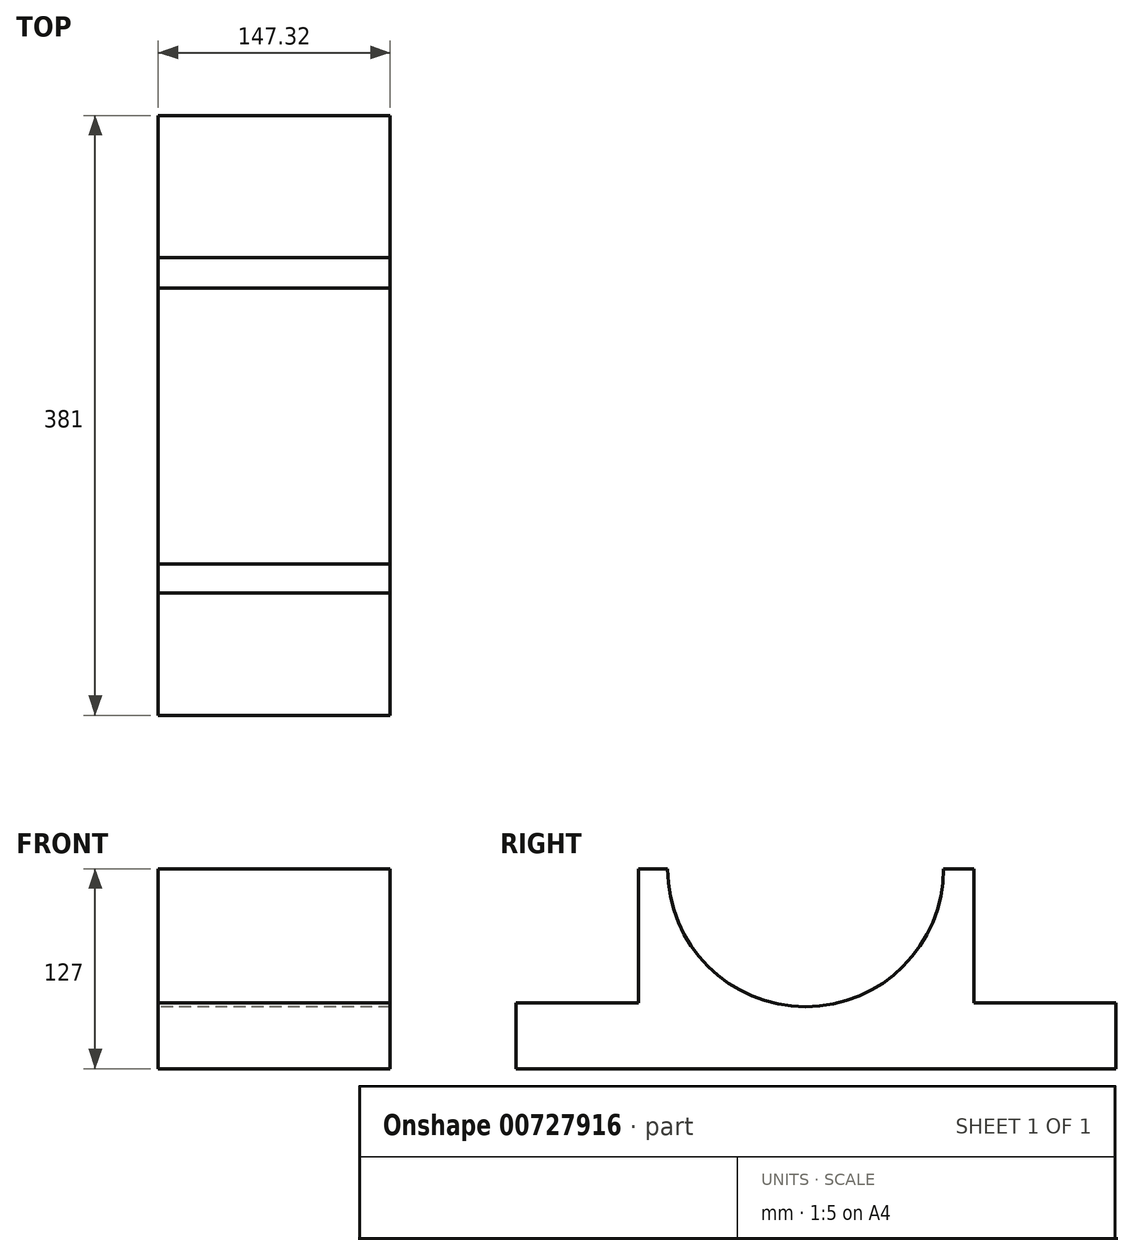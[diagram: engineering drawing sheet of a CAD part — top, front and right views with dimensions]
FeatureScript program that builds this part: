
annotation { "Feature Type Name" : "Feature", "Feature Type Description" : "" }
export const myFeature = defineFeature(function(context is Context, id is Id, definition is map)
    precondition{}
    {
        {
            var Q0;
            Q0=qCreatedBy(makeId("Right.planeOp"),FACE);
            var sketch = newSketch(context, id + "F0", { "sketchPlane" : qUnion([Q0])});
            skLineSegment(sketch, "E0.bottom", {"start": v(-190.5, 63.5) * mm, "end": v(190.5, 63.5) * mm});
            skLineSegment(sketch, "E0.top", {"start": v(-190.5, -63.5) * mm, "end": v(190.5, -63.5) * mm});
            skLineSegment(sketch, "E0.left", {"start": v(-190.5, 63.5) * mm, "end": v(-190.5, -63.5) * mm});
            skLineSegment(sketch, "E0.right", {"start": v(190.5, 63.5) * mm, "end": v(190.5, -63.5) * mm});
            skPoint(sketch, "E0.middle", {"position": v(0, 0) * mm});
            skCircle(sketch, "E1", {"center": v(-6.73, 63.5) * mm, "radius": 87.65 * mm});
            skLineSegment(sketch, "E2.bottom", {"start": v(-190.5, 63.5) * mm, "end": v(-112.72, 63.5) * mm});
            skLineSegment(sketch, "E2.top", {"start": v(-190.5, -21.67) * mm, "end": v(-112.72, -21.67) * mm});
            skLineSegment(sketch, "E2.left", {"start": v(-190.5, 63.5) * mm, "end": v(-190.5, -21.67) * mm});
            skLineSegment(sketch, "E2.right", {"start": v(-112.72, 63.5) * mm, "end": v(-112.72, -21.67) * mm});
            skLineSegment(sketch, "E3.bottom", {"start": v(190.5, 63.5) * mm, "end": v(100.1, 63.5) * mm});
            skLineSegment(sketch, "E3.top", {"start": v(190.5, -21.67) * mm, "end": v(100.1, -21.67) * mm});
            skLineSegment(sketch, "E3.left", {"start": v(190.5, 63.5) * mm, "end": v(190.5, -21.67) * mm});
            skLineSegment(sketch, "E3.right", {"start": v(100.1, 63.5) * mm, "end": v(100.1, -21.67) * mm});
            skSolve(sketch);
        }
        {
            var Q0;
            Q0=makeQuery(id+"F0.imprint","IMPRINT",FACE,{"disambiguationData":[TD([[makeQuery(id+"F0.imprint","IMPRINT",EDGE,{"derivedFrom":sQuery(id+"F0.wireOp",EDGE,"E0.top")}),1.0]])]});
            extrude(context, id + "F1", {"entities" : qUnion([Q0]), "depth" : 147.32 * mm, "offsetDistance" : 25.4 * mm});
        }
    });
